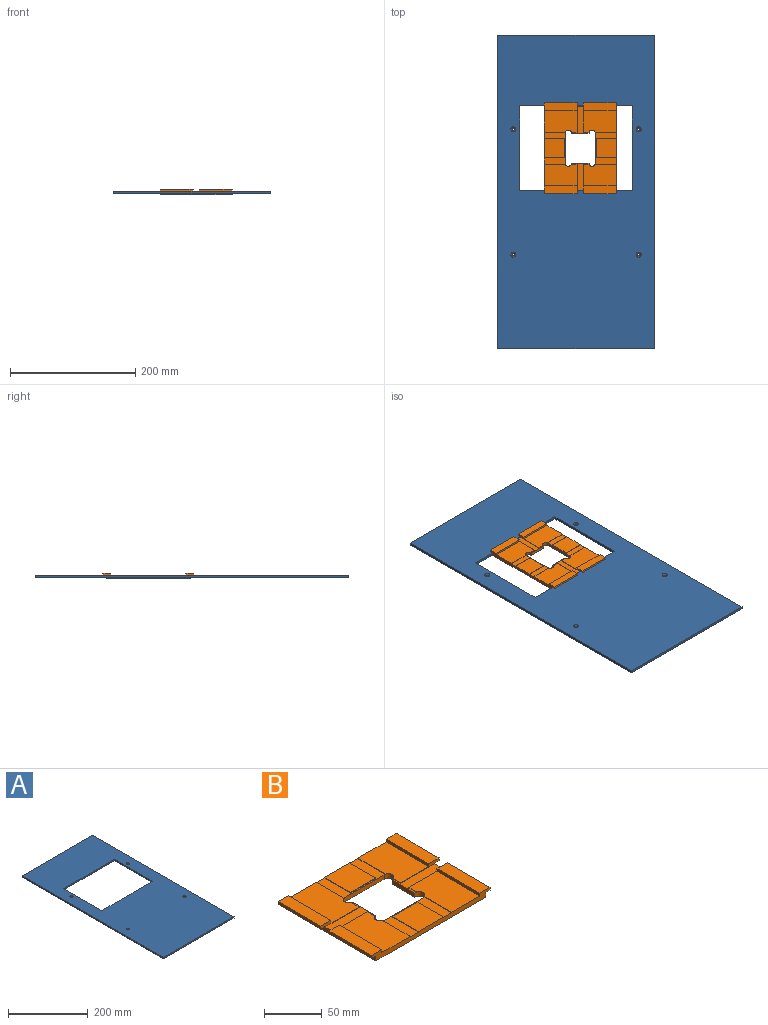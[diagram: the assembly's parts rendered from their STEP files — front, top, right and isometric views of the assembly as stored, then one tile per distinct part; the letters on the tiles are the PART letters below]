
ASSEMBLY  parts=2 mates=2
PART A: 18 faces, bbox 250x500x4 mm
  f0: cylinder r=2.25mm len=4.5mm, axis (0,0,1), area 31.8mm2, adj f5,f17
  f1: cylinder r=2.25mm len=4.5mm, axis (0,0,1), area 31.8mm2, adj f5,f16
  f2: cylinder r=2.25mm len=4.5mm, axis (0,0,1), area 31.8mm2, adj f5,f15
  f3: cylinder r=2.25mm len=4.5mm, axis (0,0,1), area 31.8mm2, adj f5,f14
  f4: plane 500x250mm, normal (0,0,1), area 100498.9mm2, adj f6,f7,f8,f9,f10,f11,f12,f13
  f5: plane 500x250mm, normal (0,0,-1), area 100636.4mm2, adj f0,f1,f2,f3,f6,f7,f8,f9
  f6: plane 500x4mm, normal (-1,0,0), area 2000mm2, adj f4,f5,f7,f9
  f7: plane 250x4mm, normal (0,-1,0), area 1000mm2, adj f4,f5,f6,f8
  f8: plane 500x4mm, normal (1,0,0), area 2000mm2, adj f4,f5,f7,f9
  f9: plane 250x4mm, normal (0,1,0), area 1000mm2, adj f4,f5,f6,f8
  f10: plane 135x4mm, normal (-1,0,0), area 540mm2, adj f4,f5,f11,f13
  f11: plane 180x4mm, normal (0,-1,0), area 720mm2, adj f4,f5,f10,f12
  f12: plane 135x4mm, normal (1,0,0), area 540mm2, adj f4,f5,f11,f13
  f13: plane 180x4mm, normal (0,1,0), area 720mm2, adj f4,f5,f10,f12
  f14: cone r=2.25mm half-angle=45deg, axis (0,0,1), area 48.6mm2, adj f3,f4
  f15: cone r=2.25mm half-angle=45deg, axis (0,0,1), area 48.6mm2, adj f2,f4
  f16: cone r=2.25mm half-angle=45deg, axis (0,0,1), area 48.6mm2, adj f1,f4
  f17: cone r=2.25mm half-angle=45deg, axis (0,0,1), area 48.6mm2, adj f0,f4
PART B: 57 faces, bbox 145x115x8 mm
  f0: plane 52.5x12.5mm, normal (0,0,1), area 656.2mm2, adj f17,f18,f31,f49
  f1: plane 52.5x12.5mm, normal (0,0,1), area 656.2mm2, adj f2,f8,f30,f55
  f2: plane 52.5x3mm, normal (1,0,0), area 157.5mm2, adj f1,f6,f8,f30
  f3: plane 52.5x3mm, normal (-1,0,0), area 157.5mm2, adj f5,f8,f24,f26
  f4: plane 52.5x12.5mm, normal (0,0,1), area 656.2mm2, adj f18,f19,f25,f51
  f5: plane 52.5x12.5mm, normal (0,0,1), area 656.2mm2, adj f3,f8,f26,f54
  f6: plane 52.5x5.1mm, normal (0,0,-1), area 267.8mm2, adj f2,f8,f21,f30
  f7: plane 52.5x5.1mm, normal (0,0,-1), area 267.8mm2, adj f18,f19,f23,f25
  f8: plane 145x8mm, normal (0,-1,0), area 739mm2, adj f1,f2,f3,f5,f6,f9,f21,f23
  f9: plane 134.8x115mm, normal (0,0,-1), area 13040.9mm2, adj f8,f10,f11,f12,f13,f14,f15,f16
  f10: plane 48x4.5mm, normal (0,1,0), area 216mm2, adj f9,f11,f20,f37
  f11: cylinder r=5mm len=10mm, axis (0,0,-1), area 77mm2, adj f9,f10,f12,f27,f29,f37,f38,f53
  f12: plane 28x4.5mm, normal (1,0,0), area 126mm2, adj f9,f11,f13,f27
  f13: cylinder r=5mm len=10mm, axis (0,0,-1), area 77mm2, adj f9,f12,f14,f27,f28,f41,f43,f50
  f14: plane 48x4.5mm, normal (0,-1,0), area 216mm2, adj f9,f13,f15,f43
  f15: cylinder r=5mm len=10mm, axis (0,0,-1), area 77mm2, adj f9,f14,f16,f32,f34,f42,f43,f48
  f16: plane 28x4.5mm, normal (-1,0,0), area 126mm2, adj f9,f15,f20,f32
  f17: plane 52.5x3mm, normal (1,0,0), area 157.5mm2, adj f0,f18,f22,f31
  f18: plane 145x8mm, normal (0,1,0), area 739mm2, adj f0,f4,f7,f9,f17,f19,f21,f22
  f19: plane 52.5x3mm, normal (-1,0,0), area 157.5mm2, adj f4,f7,f18,f25
  f20: cylinder r=5mm len=10mm, axis (0,0,-1), area 77mm2, adj f9,f10,f16,f32,f33,f36,f37,f56
  f21: plane 115x5mm, normal (1,0,0), area 570mm2, adj f6,f8,f9,f18,f22,f30,f31,f32
  f22: plane 52.5x5.1mm, normal (0,0,-1), area 267.7mm2, adj f17,f18,f21,f31
  f23: plane 115x5mm, normal (-1,0,0), area 570mm2, adj f7,f8,f9,f18,f24,f25,f26,f27
  f24: plane 52.5x5.1mm, normal (0,0,-1), area 267.7mm2, adj f3,f8,f23,f26
  f25: plane 47x3.5mm, normal (0,-1,0), area 58.5mm2, adj f4,f7,f19,f23,f27,f28,f50,f51
  f26: plane 47x3.5mm, normal (0,1,0), area 58.5mm2, adj f3,f5,f23,f24,f27,f29,f53,f54
  f27: plane 43.4x28.46mm, normal (0,0,1), area 461.2mm2, adj f11,f12,f13,f23,f25,f26,f28,f29
  f28: plane 9.23x0.5mm, normal (1,0,0), area 4.6mm2, adj f13,f25,f27,f50
  f29: plane 9.23x0.5mm, normal (1,0,0), area 4.6mm2, adj f11,f26,f27,f53
  f30: plane 47x3.5mm, normal (0,1,0), area 58.5mm2, adj f1,f2,f6,f21,f32,f33,f55,f56
  f31: plane 47x3.5mm, normal (0,-1,0), area 58.5mm2, adj f0,f17,f21,f22,f32,f34,f48,f49
  f32: plane 43.4x28.46mm, normal (0,0,1), area 461.2mm2, adj f15,f16,f20,f21,f30,f31,f33,f34
  f33: plane 9.23x0.5mm, normal (-1,0,0), area 4.6mm2, adj f20,f30,f32,f56
  f34: plane 9.23x0.5mm, normal (-1,0,0), area 4.6mm2, adj f15,f31,f32,f48
  f35: plane 31x0.5mm, normal (0,1,0), area 15.5mm2, adj f37,f39,f40,f52
  f36: plane 33.73x0.5mm, normal (-1,0,0), area 16.9mm2, adj f8,f20,f37,f56
  f37: plane 51x33.73mm, normal (0,0,1), area 716.7mm2, adj f8,f10,f11,f20,f35,f36,f38,f39
  f38: plane 33.73x0.5mm, normal (1,0,0), area 16.9mm2, adj f8,f11,f37,f53
  f39: plane 32x0.5mm, normal (1,0,0), area 16mm2, adj f8,f35,f37,f52
  f40: plane 32x0.5mm, normal (-1,0,0), area 16mm2, adj f8,f35,f37,f52
  f41: plane 33.73x0.5mm, normal (1,0,0), area 16.9mm2, adj f13,f18,f43,f50
  f42: plane 33.73x0.5mm, normal (-1,0,0), area 16.9mm2, adj f15,f18,f43,f48
  f43: plane 51x33.73mm, normal (0,0,1), area 716.7mm2, adj f13,f14,f15,f18,f41,f42,f44,f45
  f44: plane 32x0.5mm, normal (1,0,0), area 16mm2, adj f18,f43,f45,f47
  f45: plane 31x0.5mm, normal (0,-1,0), area 15.5mm2, adj f43,f44,f46,f47
  f46: plane 32x0.5mm, normal (-1,0,0), area 16mm2, adj f18,f43,f45,f47
  f47: plane 32x31mm, normal (0,0,1), area 992mm2, adj f18,f44,f45,f46
  f48: plane 52.5x34.5mm, normal (0,0,1), area 1786.8mm2, adj f15,f18,f31,f34,f42,f49
  f49: plane 52.5x3mm, normal (-1,0,0), area 157.5mm2, adj f0,f18,f31,f48
  f50: plane 52.5x34.5mm, normal (0,0,1), area 1786.8mm2, adj f13,f18,f25,f28,f41,f51
  f51: plane 52.5x3mm, normal (1,0,0), area 157.5mm2, adj f4,f18,f25,f50
  f52: plane 32x31mm, normal (0,0,1), area 992mm2, adj f8,f35,f39,f40
  f53: plane 52.5x34.5mm, normal (0,0,1), area 1786.8mm2, adj f8,f11,f26,f29,f38,f54
  f54: plane 52.5x3mm, normal (1,0,0), area 157.5mm2, adj f5,f8,f26,f53
  f55: plane 52.5x3mm, normal (-1,0,0), area 157.5mm2, adj f1,f8,f30,f56
  f56: plane 52.5x34.5mm, normal (0,0,1), area 1786.8mm2, adj f8,f20,f30,f33,f36,f55
PLACE A t=(31.18,-101.98,69.17)mm
PLACE B rot(axis=(0,0,1),90deg) t=(162.95,217.92,68.17)mm
MATE planar B.f23 <-> A.f13  axis (0,-1,0) through (162.95,150.52,70.65)mm
MATE planar B.f7 <-> A.f4  axis (0,0,-1) through (131.7,147.97,73.17)mm
